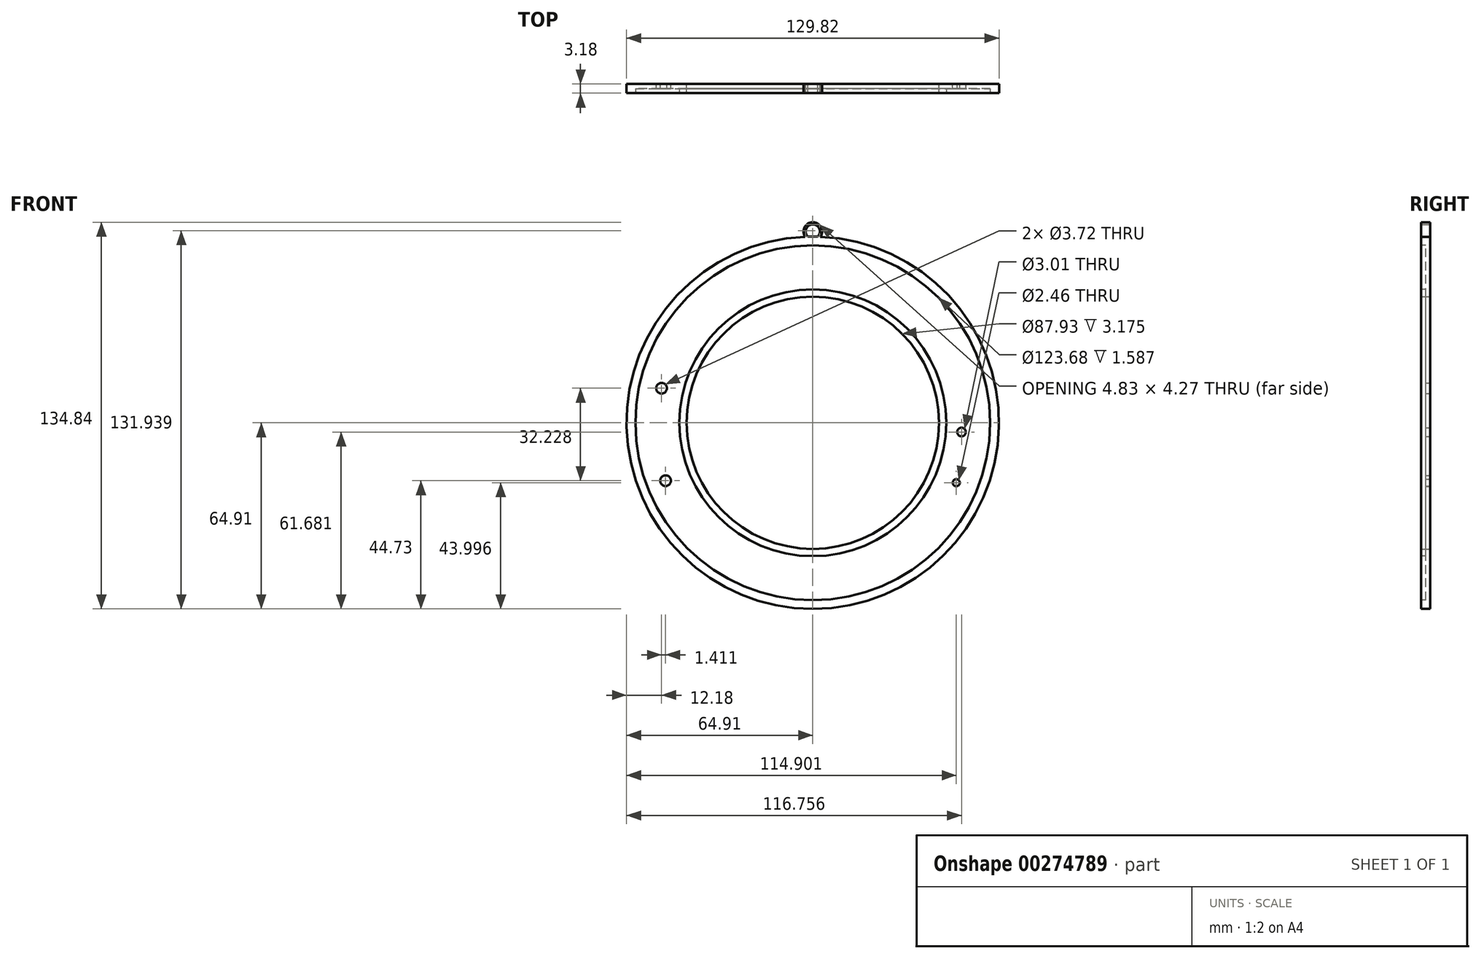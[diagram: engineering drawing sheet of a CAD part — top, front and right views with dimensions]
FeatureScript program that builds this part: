
annotation { "Feature Type Name" : "Feature", "Feature Type Description" : "" }
export const myFeature = defineFeature(function(context is Context, id is Id, definition is map)
    precondition{}
    {
        {
            var Q0;
            Q0=qCreatedBy(makeId("Front.planeOp"),FACE);
            var sketch = newSketch(context, id + "F0", { "sketchPlane" : qUnion([Q0])});
            skCircle(sketch, "E0", {"center": v(0, 0) * mm, "radius": 64.91 * mm});
            skCircle(sketch, "E1", {"center": v(0, 0) * mm, "radius": 43.97 * mm});
            skCircle(sketch, "E2", {"center": v(-51.32, -20.18) * mm, "radius": 1.86 * mm});
            skCircle(sketch, "E3", {"center": v(-52.73, 12.05) * mm, "radius": 1.86 * mm});
            skCircle(sketch, "E4", {"center": v(50, -20.91) * mm, "radius": 1.23 * mm});
            skCircle(sketch, "E5", {"center": v(51.85, -3.23) * mm, "radius": 1.5 * mm});
            skCircle(sketch, "E6", {"center": v(0, 66.7) * mm, "radius": 2.48 * mm});
            skCircle(sketch, "E7", {"center": v(0, 66.7) * mm, "radius": 3.24 * mm});
            skSolve(sketch);
        }
        {
            var Q0;
            Q0=makeQuery(id+"F0.imprint","IMPRINT",FACE,{"disambiguationData":[TD([[makeQuery(id+"F0.imprint","IMPRINT",EDGE,{"derivedFrom":sQuery(id+"F0.wireOp",EDGE,"E1")}),-1.0]])]});
            var Q1;
            {var subQ0=sQuery(id+"F0.wireOp",EDGE,"E7");var subQ1=sQuery(id+"F0.wireOp",EDGE,"E0");var subQ2=makeQuery(id+"F0.imprint","INTERSECT",VERTEX,{"disambiguationData":[OD(0.0)],"derivedFrom":[subQ1,subQ0]});Q1=makeQuery(id+"F0.imprint","IMPRINT",FACE,{"disambiguationData":[TD([[makeQuery(id+"F0.imprint","IMPRINT",EDGE,{"disambiguationData":[TD([[subQ2,-1.0]])],"derivedFrom":subQ1}),1.0]])]});}
            var Q2;
            {var subQ0=sQuery(id+"F0.wireOp",EDGE,"E6");var subQ1=sQuery(id+"F0.wireOp",EDGE,"E0");var subQ2=makeQuery(id+"F0.imprint","INTERSECT",VERTEX,{"disambiguationData":[OD(0.0)],"derivedFrom":[subQ1,subQ0]});Q2=makeQuery(id+"F0.imprint","IMPRINT",FACE,{"disambiguationData":[TD([[makeQuery(id+"F0.imprint","IMPRINT",EDGE,{"disambiguationData":[TD([[subQ2,-1.0]])],"derivedFrom":subQ1}),1.0]])]});}
            var Q3;
            {var subQ0=sQuery(id+"F0.wireOp",EDGE,"E7");var subQ1=sQuery(id+"F0.wireOp",EDGE,"E0");var subQ2=makeQuery(id+"F0.imprint","INTERSECT",VERTEX,{"disambiguationData":[OD(0.0)],"derivedFrom":[subQ1,subQ0]});Q3=makeQuery(id+"F0.imprint","IMPRINT",FACE,{"disambiguationData":[TD([[makeQuery(id+"F0.imprint","IMPRINT",EDGE,{"disambiguationData":[TD([[subQ2,-1.0]])],"derivedFrom":subQ1}),-1.0]])]});}
            extrude(context, id + "F1", {"entities" : qUnion([Q0, Q1, Q2, Q3]), "depth" : 3.17 * mm});
        }
        {
            var Q0;
            Q0=makeQuery(id+"F1.opExtrude","CAP_FACE",FACE,{"disambiguationData":[OSD([sQuery(id+"F0.wireOp",EDGE,"E0"),sQuery(id+"F0.wireOp",EDGE,"E1"),sQuery(id+"F0.wireOp",EDGE,"E2"),sQuery(id+"F0.wireOp",EDGE,"E3"),sQuery(id+"F0.wireOp",EDGE,"E4"),sQuery(id+"F0.wireOp",EDGE,"E5"),sQuery(id+"F0.wireOp",EDGE,"E6"),sQuery(id+"F0.wireOp",EDGE,"E7")])],"isStart":false});
            var sketch = newSketch(context, id + "F2", { "sketchPlane" : qUnion([Q0])});
            skCircle(sketch, "E8", {"center": v(0, 0) * mm, "radius": 61.84 * mm});
            skCircle(sketch, "E9", {"center": v(0, 0) * mm, "radius": 46.5 * mm});
            skSolve(sketch);
        }
        {
            var Q0;
            Q0=makeQuery(id+"F2.imprint","IMPRINT",FACE,{"disambiguationData":[TD([[makeQuery(id+"F2.imprint","IMPRINT",EDGE,{"derivedFrom":sQuery(id+"F2.wireOp",EDGE,"E8")}),1.0]])]});
            extrude(context, id + "F3", {"entities" : qUnion([Q0]), "operationType" : NewBodyOperationType.REMOVE, "oppositeDirection" : true, "depth" : 1.59 * mm});
        }
    });
